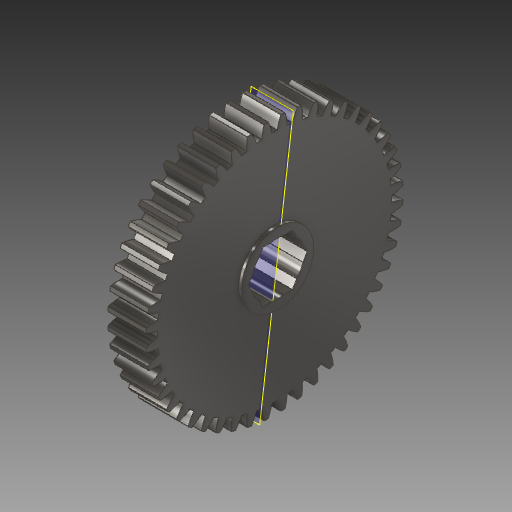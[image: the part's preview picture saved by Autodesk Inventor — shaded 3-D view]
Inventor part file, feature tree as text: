
AUTODESK INVENTOR PART (.ipt)
format: ipt  version: 2017.1 (Build 211199000, 199)  size: 460,288 bytes
history: native  units: in
note: dims shown in document units (in); Inventor stores cm internally (conversion verified against a paired STEP export)
features: plane x1, other x1
ambient origin geometry x8: Origin, YZ Plane, XZ Plane, XY Plane, X Axis, Y Axis, Z Axis, Center Point
bodies: Solid1 (feature_tree)
feature tree (2):
  plane  "Work Plane2"
  other  "Bore"
